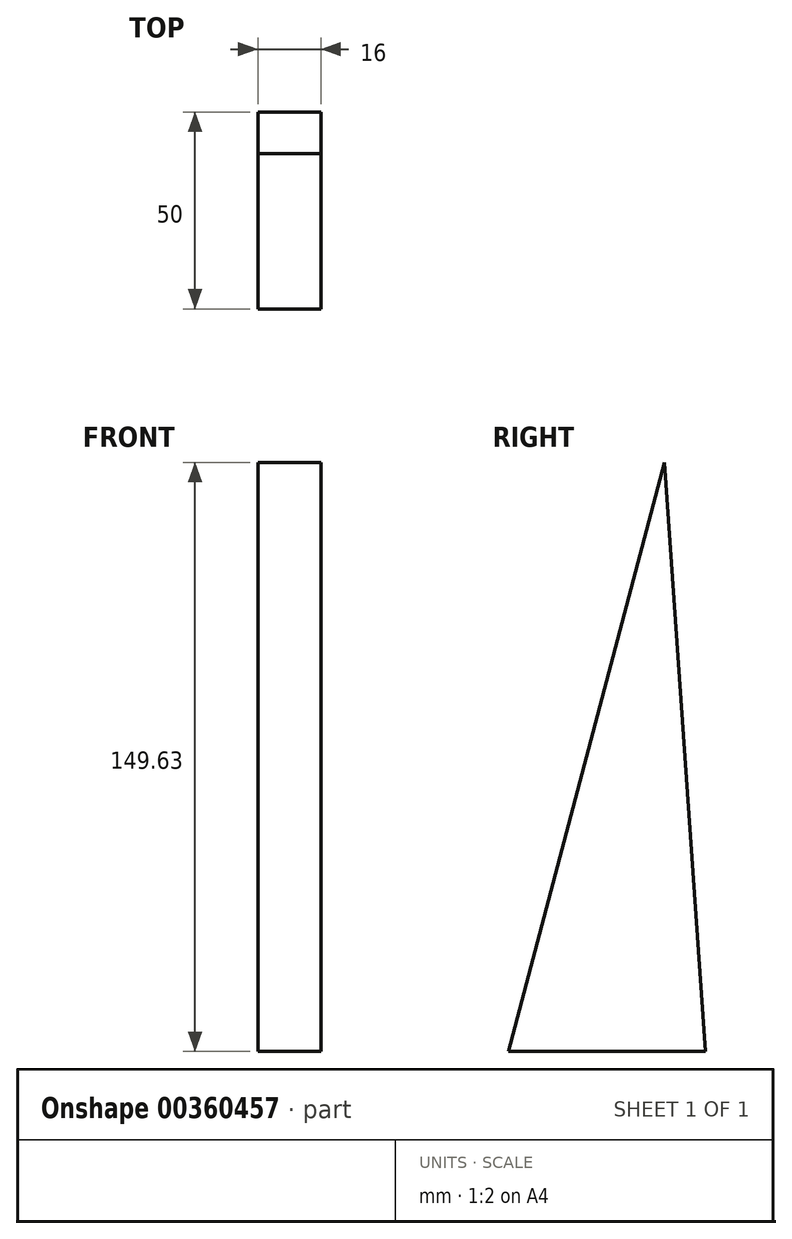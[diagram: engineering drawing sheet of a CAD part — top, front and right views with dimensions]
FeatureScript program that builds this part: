
annotation { "Feature Type Name" : "Feature", "Feature Type Description" : "" }
export const myFeature = defineFeature(function(context is Context, id is Id, definition is map)
    precondition{}
    {
        {
            var Q0;
            Q0=qCreatedBy(makeId("Right.planeOp"),FACE);
            var sketch = newSketch(context, id + "F0", { "sketchPlane" : qUnion([Q0])});
            skLineSegment(sketch, "E0", {"start": v(0, 0) * mm, "end": v(-10.46, 149.63) * mm});
            skLineSegment(sketch, "E1", {"start": v(-10.46, 149.63) * mm, "end": v(-50, 0) * mm});
            skLineSegment(sketch, "E2", {"start": v(-50, 0) * mm, "end": v(0, 0) * mm});
            skSolve(sketch);
        }
        {
            var Q0;
            Q0=makeQuery(id+"F0.imprint","IMPRINT",FACE,{"disambiguationData":[TD([[makeQuery(id+"F0.imprint","IMPRINT",EDGE,{"derivedFrom":sQuery(id+"F0.wireOp",EDGE,"E0")}),1.0]])]});
            extrude(context, id + "F1", {"entities" : qUnion([Q0]), "endBound" : BoundingType.SYMMETRIC, "depth" : 16 * mm});
        }
    });
